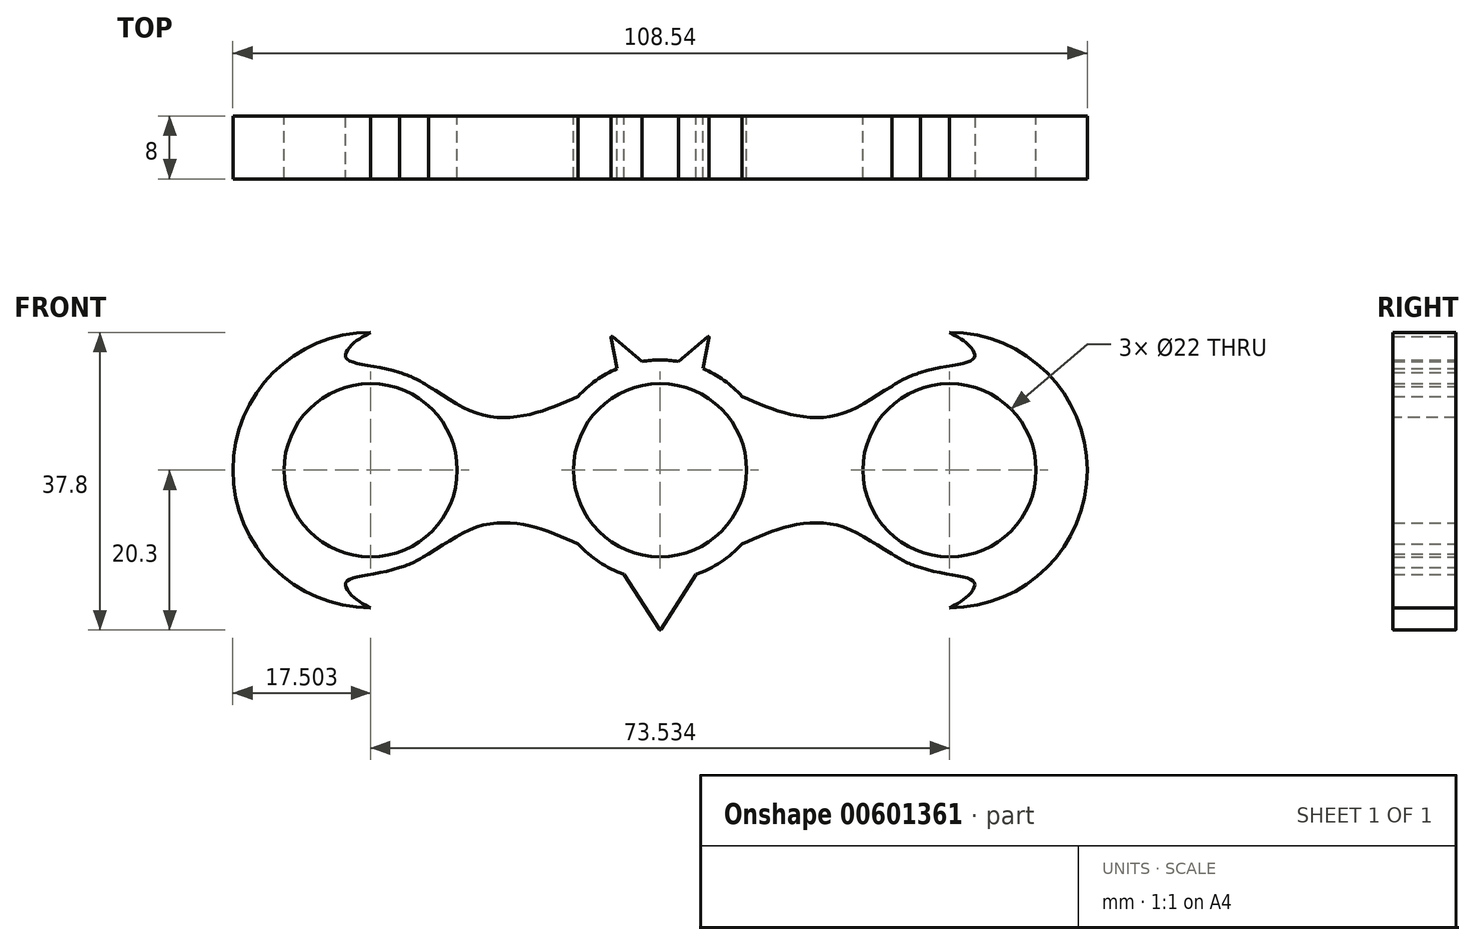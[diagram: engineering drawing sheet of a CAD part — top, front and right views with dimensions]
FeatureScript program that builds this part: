
annotation { "Feature Type Name" : "Feature", "Feature Type Description" : "" }
export const myFeature = defineFeature(function(context is Context, id is Id, definition is map)
    precondition{}
    {
        {
            var Q0;
            Q0=qCreatedBy(makeId("Front.planeOp"),FACE);
            var sketch = newSketch(context, id + "F0", { "sketchPlane" : qUnion([Q0])});
            skCircle(sketch, "E0", {"center": v(0, 0) * mm, "radius": 11 * mm});
            skCircle(sketch, "E1.0", {"center": v(0, 0) * mm, "radius": 3 * mm});
            skCircle(sketch, "E2.0", {"center": v(0, 0) * mm, "radius": 14 * mm});
            skArc(sketch, "E3", {"start": v(-36.78, 17.5) * mm, "mid": v(-54.27, 0) * mm, "end": v(-36.78, -17.5) * mm});
            skCircle(sketch, "E4", {"center": v(-36.77, 0) * mm, "radius": 11 * mm});
            skCircle(sketch, "E5", {"center": v(-36.77, 0) * mm, "radius": 12.92 * mm});
            skLineSegment(sketch, "E6", {"start": v(-0.1, -20.25) * mm, "end": v(-4.58, -13.23) * mm});
            skLineSegment(sketch, "E7", {"start": v(-5.46, 12.9) * mm, "end": v(-6.24, 16.84) * mm});
            skLineSegment(sketch, "E8", {"start": v(-6.06, 16.95) * mm, "end": v(-2.31, 13.8) * mm});
            skPoint(sketch, "E9.visualSharp", {"position": v(-6.3, 17.15) * mm});
            skArc(sketch, "E9.filletArc", {"start": v(-6.06, 16.95) * mm, "mid": v(-6.19, 16.96) * mm, "end": v(-6.24, 16.84) * mm});
            skFitSpline(sketch, "E10", {"points": [v(-36.78, 17.5) * mm, v(-39.08, 15.99) * mm, v(-39.91, 14.26) * mm, v(-33.09, 12.39) * mm, v(-23.75, 7.4) * mm, v(-16.62, 7.07) * mm, v(-10.4, 9.37) * mm], "startDerivative": vector(-20.57, -10.94) * mm, "endDerivative": vector(33.44, 14.83) * mm});
            skFitSpline(sketch, "E11.MirrorCS", {"points": [v(-36.78, -17.5) * mm, v(-39.08, -15.99) * mm, v(-39.91, -14.26) * mm, v(-33.09, -12.39) * mm, v(-23.75, -7.4) * mm, v(-16.62, -7.07) * mm, v(-10.4, -9.37) * mm], "startDerivative": vector(-20.57, 10.94) * mm, "endDerivative": vector(33.44, -14.83) * mm});
            skPoint(sketch, "E12.orphan", {"position": v(-58.25, 0) * mm});
            skFitSpline(sketch, "E13.MirrorCS", {"points": [v(36.78, -17.5) * mm, v(39.08, -15.99) * mm, v(39.91, -14.26) * mm, v(33.09, -12.39) * mm, v(23.75, -7.4) * mm, v(16.62, -7.07) * mm, v(10.4, -9.37) * mm], "startDerivative": vector(20.57, 10.94) * mm, "endDerivative": vector(-33.44, -14.83) * mm});
            skPoint(sketch, "E14.MirrorP", {"position": v(58.25, 0) * mm});
            skCircle(sketch, "E15.MirrorC", {"center": v(36.77, 0) * mm, "radius": 12.92 * mm});
            skCircle(sketch, "E16.MirrorC", {"center": v(36.77, 0) * mm, "radius": 11 * mm});
            skFitSpline(sketch, "E17.MirrorCS", {"points": [v(36.78, 17.5) * mm, v(39.08, 15.99) * mm, v(39.91, 14.26) * mm, v(33.09, 12.39) * mm, v(23.75, 7.4) * mm, v(16.62, 7.07) * mm, v(10.4, 9.37) * mm], "startDerivative": vector(20.57, -10.94) * mm, "endDerivative": vector(-33.44, 14.83) * mm});
            skArc(sketch, "E18.MirrorCS", {"start": v(36.78, 17.5) * mm, "mid": v(54.27, 0) * mm, "end": v(36.78, -17.5) * mm});
            skArc(sketch, "E19.MirrorCS", {"start": v(6.06, 16.95) * mm, "mid": v(6.19, 16.96) * mm, "end": v(6.24, 16.84) * mm});
            skPoint(sketch, "E20.MirrorP", {"position": v(6.3, 17.15) * mm});
            skLineSegment(sketch, "E21.MirrorCS", {"start": v(6.06, 16.95) * mm, "end": v(2.31, 13.8) * mm});
            skLineSegment(sketch, "E22.MirrorCS", {"start": v(5.46, 12.9) * mm, "end": v(6.24, 16.84) * mm});
            skLineSegment(sketch, "E23.MirrorCS", {"start": v(0.1, -20.25) * mm, "end": v(4.58, -13.23) * mm});
            skPoint(sketch, "E24.start.orphan", {"position": v(0, -38.5) * mm});
            skPoint(sketch, "E25.visualSharp", {"position": v(0, -20.39) * mm});
            skArc(sketch, "E25.filletArc", {"start": v(-0.1, -20.25) * mm, "mid": v(0, -20.3) * mm, "end": v(0.1, -20.25) * mm});
            skSolve(sketch);
        }
        {
            var Q0;
            Q0=qSketchRegion(id+"F0",true);
            extrude(context, id + "F1", {"entities" : qUnion([Q0]), "depth" : 8 * mm, "offsetDistance" : 25 * mm});
        }
    });
